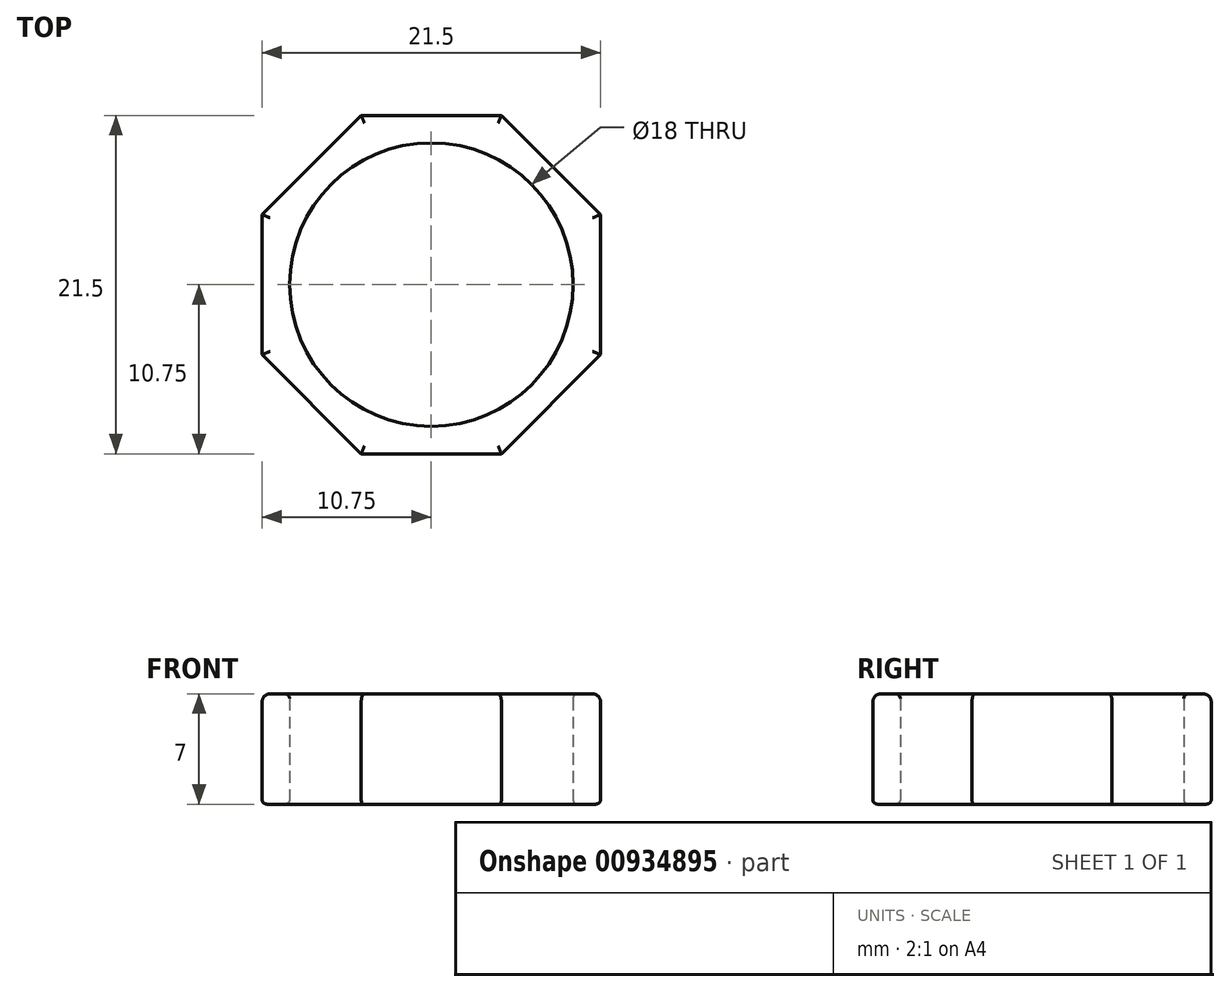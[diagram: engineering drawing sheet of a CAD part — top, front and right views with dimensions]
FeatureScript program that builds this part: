
annotation { "Feature Type Name" : "Feature", "Feature Type Description" : "" }
export const myFeature = defineFeature(function(context is Context, id is Id, definition is map)
    precondition{}
    {
        {
            assignVariable(context, id + "F0", {"name" : "height", "anyValue" : 7});
        }
        {
            var Q0;
            Q0=qCreatedBy(makeId("Top.planeOp"),FACE);
            var sketch = newSketch(context, id + "F1", { "sketchPlane" : qUnion([Q0])});
            skCircle(sketch, "E0", {"center": v(0, 0) * mm, "radius": 9 * mm});
            skCircle(sketch, "E1", {"center": v(0, 0) * mm, "radius": 10.75 * mm, "construction": true});
            skArc(sketch, "E2.cCircle", {"start": v(-10.75, 0) * mm, "mid": v(9.93, -4.11) * mm, "end": v(-7.6, 7.6) * mm, "construction": true});
            skLineSegment(sketch, "E2.0", {"start": v(-4.45, 10.75) * mm, "end": v(4.45, 10.75) * mm});
            skLineSegment(sketch, "E2.1", {"start": v(4.45, 10.75) * mm, "end": v(10.75, 4.45) * mm});
            skLineSegment(sketch, "E2.2", {"start": v(10.75, 4.45) * mm, "end": v(10.75, -4.45) * mm});
            skLineSegment(sketch, "E2.3", {"start": v(10.75, -4.45) * mm, "end": v(4.45, -10.75) * mm});
            skLineSegment(sketch, "E2.4", {"start": v(4.45, -10.75) * mm, "end": v(-4.45, -10.75) * mm});
            skLineSegment(sketch, "E2.5", {"start": v(-4.45, -10.75) * mm, "end": v(-10.75, -4.45) * mm});
            skLineSegment(sketch, "E2.6", {"start": v(-10.75, -4.45) * mm, "end": v(-10.75, 4.45) * mm});
            skLineSegment(sketch, "E2.7", {"start": v(-10.75, 4.45) * mm, "end": v(-4.45, 10.75) * mm});
            skPoint(sketch, "E2.0.midPoint", {"position": v(0, 10.75) * mm});
            skSolve(sketch);
        }
        {
            var Q0;
            Q0=makeQuery(id+"F1.imprint","IMPRINT",FACE,{"disambiguationData":[TD([[makeQuery(id+"F1.imprint","IMPRINT",EDGE,{"derivedFrom":sQuery(id+"F1.wireOp",EDGE,"E0")}),-1.0]])]});
            extrude(context, id + "F2", {"entities" : qUnion([Q0]), "depth" : (getVariable(context, 'height')) * mm, "offsetDistance" : 25 * mm});
        }
        {
            var Q0;
            Q0=makeQuery(id+"F2.opExtrude","CAP_EDGE",EDGE,{"disambiguationData":[OSD([sQuery(id+"F1.wireOp",EDGE,"E2.1")])],"isStart":false});
            var Q1;
            Q1=makeQuery(id+"F2.opExtrude","CAP_EDGE",EDGE,{"disambiguationData":[OSD([sQuery(id+"F1.wireOp",EDGE,"E2.0")])],"isStart":false});
            var Q2;
            Q2=makeQuery(id+"F2.opExtrude","CAP_EDGE",EDGE,{"disambiguationData":[OSD([sQuery(id+"F1.wireOp",EDGE,"E2.7")])],"isStart":false});
            var Q3;
            Q3=makeQuery(id+"F2.opExtrude","CAP_EDGE",EDGE,{"disambiguationData":[OSD([sQuery(id+"F1.wireOp",EDGE,"E2.6")])],"isStart":false});
            var Q4;
            Q4=makeQuery(id+"F2.opExtrude","CAP_EDGE",EDGE,{"disambiguationData":[OSD([sQuery(id+"F1.wireOp",EDGE,"E2.5")])],"isStart":false});
            var Q5;
            Q5=makeQuery(id+"F2.opExtrude","CAP_EDGE",EDGE,{"disambiguationData":[OSD([sQuery(id+"F1.wireOp",EDGE,"E2.4")])],"isStart":false});
            var Q6;
            Q6=makeQuery(id+"F2.opExtrude","CAP_EDGE",EDGE,{"disambiguationData":[OSD([sQuery(id+"F1.wireOp",EDGE,"E2.3")])],"isStart":false});
            var Q7;
            Q7=makeQuery(id+"F2.opExtrude","CAP_EDGE",EDGE,{"disambiguationData":[OSD([sQuery(id+"F1.wireOp",EDGE,"E2.2")])],"isStart":false});
            fillet(context, id + "F3", {"entities" : qUnion([Q0, Q1, Q2, Q3, Q4, Q5, Q6, Q7]), "radius" : .5 * mm, "tangentPropagation" : true, "allowEdgeOverflow" : false});
        }
        {
            var Q0;
            Q0=makeQuery(id+"F2.opExtrude","CAP_EDGE",EDGE,{"disambiguationData":[OSD([sQuery(id+"F1.wireOp",EDGE,"E2.4")])],"isStart":true});
            var Q1;
            Q1=makeQuery(id+"F2.opExtrude","CAP_EDGE",EDGE,{"disambiguationData":[OSD([sQuery(id+"F1.wireOp",EDGE,"E2.5")])],"isStart":true});
            var Q2;
            Q2=makeQuery(id+"F2.opExtrude","CAP_EDGE",EDGE,{"disambiguationData":[OSD([sQuery(id+"F1.wireOp",EDGE,"E2.6")])],"isStart":true});
            var Q3;
            Q3=makeQuery(id+"F2.opExtrude","CAP_EDGE",EDGE,{"disambiguationData":[OSD([sQuery(id+"F1.wireOp",EDGE,"E2.7")])],"isStart":true});
            var Q4;
            Q4=makeQuery(id+"F2.opExtrude","CAP_EDGE",EDGE,{"disambiguationData":[OSD([sQuery(id+"F1.wireOp",EDGE,"E2.0")])],"isStart":true});
            var Q5;
            Q5=makeQuery(id+"F2.opExtrude","CAP_EDGE",EDGE,{"disambiguationData":[OSD([sQuery(id+"F1.wireOp",EDGE,"E2.1")])],"isStart":true});
            var Q6;
            Q6=makeQuery(id+"F2.opExtrude","CAP_EDGE",EDGE,{"disambiguationData":[OSD([sQuery(id+"F1.wireOp",EDGE,"E2.2")])],"isStart":true});
            var Q7;
            Q7=makeQuery(id+"F2.opExtrude","CAP_EDGE",EDGE,{"disambiguationData":[OSD([sQuery(id+"F1.wireOp",EDGE,"E2.3")])],"isStart":true});
            fillet(context, id + "F4", {"entities" : qUnion([Q0, Q1, Q2, Q3, Q4, Q5, Q6, Q7]), "radius" : .3 * mm, "tangentPropagation" : true, "allowEdgeOverflow" : false});
        }
        {
            var Q0;
            Q0=makeQuery(id+"F2.opExtrude","CAP_EDGE",EDGE,{"disambiguationData":[OSD([sQuery(id+"F1.wireOp",EDGE,"E0")])],"isStart":true});
            fillet(context, id + "F5", {"entities" : qUnion([Q0]), "radius" : .3 * mm, "tangentPropagation" : true, "allowEdgeOverflow" : false});
        }
        {
            var Q0;
            Q0=makeQuery(id+"F2.opExtrude","CAP_EDGE",EDGE,{"disambiguationData":[OSD([sQuery(id+"F1.wireOp",EDGE,"E0")])],"isStart":false});
            fillet(context, id + "F6", {"entities" : qUnion([Q0]), "radius" : .3 * mm, "tangentPropagation" : true, "allowEdgeOverflow" : false});
        }
    });
